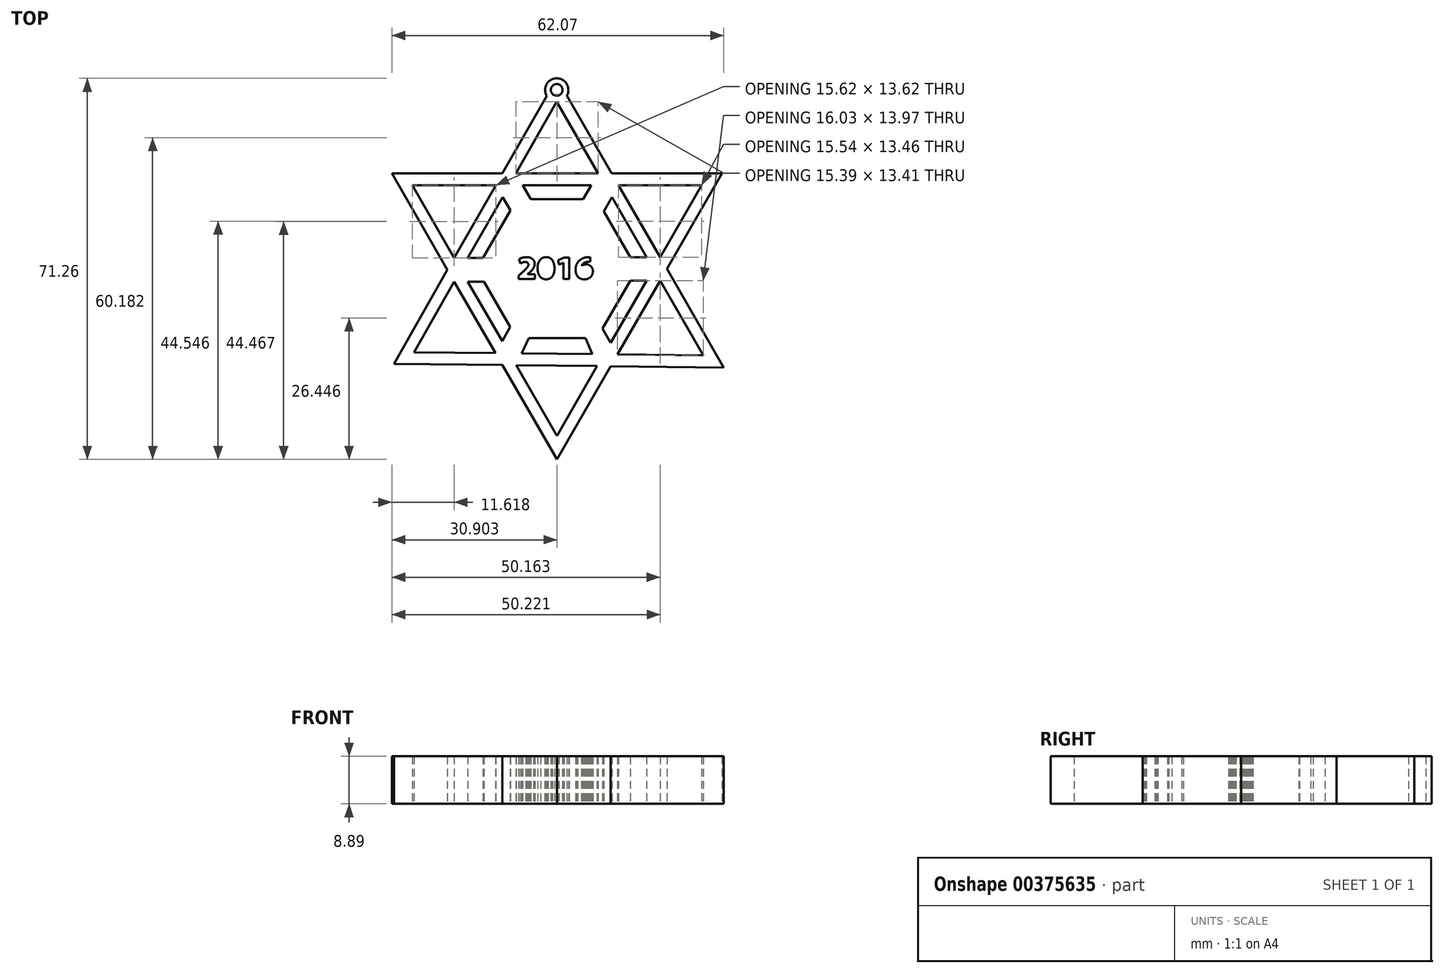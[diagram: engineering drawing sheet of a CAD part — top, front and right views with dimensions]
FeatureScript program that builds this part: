
annotation { "Feature Type Name" : "Feature", "Feature Type Description" : "" }
export const myFeature = defineFeature(function(context is Context, id is Id, definition is map)
    precondition{}
    {
        {
            var Q0;
            Q0=qCreatedBy(makeId("Top.planeOp"),FACE);
            var sketch = newSketch(context, id + "F0", { "sketchPlane" : qUnion([Q0])});
            skLineSegment(sketch, "E0.0", {"start": v(-30.87, 17.82) * mm, "end": v(-10.19, 17.82) * mm});
            skLineSegment(sketch, "E0.1", {"start": v(30.87, 17.82) * mm, "end": v(20.56, -0.03) * mm});
            skLineSegment(sketch, "E0.2", {"start": v(0, -35.65) * mm, "end": v(-10.19, -18) * mm});
            skPoint(sketch, "E0.0.midPoint", {"position": v(0, 17.82) * mm});
            skLineSegment(sketch, "E1.0", {"start": v(31.2, -18.45) * mm, "end": v(10.06, -18.22) * mm});
            skLineSegment(sketch, "E1.1", {"start": v(-30.48, -17.78) * mm, "end": v(-20.46, -0.2) * mm});
            skLineSegment(sketch, "E1.2", {"start": v(-0.03, 35.64) * mm, "end": v(-0.02, 35.61) * mm});
            skLineSegment(sketch, "E2", {"start": v(-27.06, 15.62) * mm, "end": v(-19.2, 2) * mm});
            skLineSegment(sketch, "E3", {"start": v(-27.06, 15.62) * mm, "end": v(-11.44, 15.62) * mm});
            skLineSegment(sketch, "E4", {"start": v(-26.72, -15.6) * mm, "end": v(-19.2, -2.4) * mm});
            skLineSegment(sketch, "E5", {"start": v(-0.02, 31.24) * mm, "end": v(7.73, 17.82) * mm});
            skLineSegment(sketch, "E6", {"start": v(-26.72, -15.6) * mm, "end": v(-11.48, -15.77) * mm});
            skLineSegment(sketch, "E7", {"start": v(27.06, 15.62) * mm, "end": v(19.3, 2.17) * mm});
            skLineSegment(sketch, "E8.trimOffspring", {"start": v(-20.46, -0.2) * mm, "end": v(-30.87, 17.82) * mm});
            skLineSegment(sketch, "E9.trimOffspring", {"start": v(-16.68, 2) * mm, "end": v(-10.17, 13.43) * mm});
            skLineSegment(sketch, "E10.trimOffspring", {"start": v(-16.65, -2.4) * mm, "end": v(-10.23, -13.54) * mm});
            skLineSegment(sketch, "E11.trimOffspring", {"start": v(-19.2, 2) * mm, "end": v(-11.44, 15.62) * mm});
            skPoint(sketch, "E12.orphan", {"position": v(-28.33, 17.82) * mm});
            skLineSegment(sketch, "E13.trimOffspring", {"start": v(-10.19, 17.82) * mm, "end": v(-1.9, 32.35) * mm});
            skLineSegment(sketch, "E14.trimOffspring", {"start": v(-6.4, 15.62) * mm, "end": v(6.46, 15.62) * mm});
            skLineSegment(sketch, "E15.trimOffspring", {"start": v(-7.66, 17.82) * mm, "end": v(-0.02, 31.24) * mm});
            skLineSegment(sketch, "E16.trimOffspring", {"start": v(-7.66, 17.82) * mm, "end": v(7.73, 17.82) * mm});
            skPoint(sketch, "E17.orphan", {"position": v(-1.29, 33.44) * mm});
            skPoint(sketch, "E18.orphan", {"position": v(1.24, 33.44) * mm});
            skLineSegment(sketch, "E19.trimOffspring", {"start": v(10.25, 17.82) * mm, "end": v(30.87, 17.82) * mm});
            skLineSegment(sketch, "E20.trimOffspring", {"start": v(11.52, 15.62) * mm, "end": v(27.06, 15.62) * mm});
            skLineSegment(sketch, "E21.trimOffspring", {"start": v(11.52, 15.62) * mm, "end": v(19.3, 2.17) * mm});
            skLineSegment(sketch, "E22.trimOffspring", {"start": v(10.28, 13.4) * mm, "end": v(16.77, 2.17) * mm});
            skPoint(sketch, "E23.orphan", {"position": v(28.33, 17.82) * mm});
            skPoint(sketch, "E24.orphan", {"position": v(29.6, 15.62) * mm});
            skLineSegment(sketch, "E25.trimOffspring", {"start": v(20.56, -0.03) * mm, "end": v(31.2, -18.45) * mm});
            skLineSegment(sketch, "E26.trimOffspring", {"start": v(19.3, -2.22) * mm, "end": v(27.37, -16.19) * mm});
            skLineSegment(sketch, "E27.trimOffspring", {"start": v(19.3, -2.22) * mm, "end": v(11.34, -16.02) * mm});
            skLineSegment(sketch, "E28.trimOffspring", {"start": v(16.76, -2.22) * mm, "end": v(10.06, -13.82) * mm});
            skPoint(sketch, "E29.orphan", {"position": v(28.66, -18.42) * mm});
            skLineSegment(sketch, "E30.trimOffspring", {"start": v(10.06, -18.22) * mm, "end": v(0, -35.65) * mm});
            skLineSegment(sketch, "E31.trimOffspring", {"start": v(7.54, -18.2) * mm, "end": v(0, -31.25) * mm});
            skLineSegment(sketch, "E32.trimOffspring", {"start": v(11.34, -16.02) * mm, "end": v(27.37, -16.19) * mm});
            skLineSegment(sketch, "E33.trimOffspring", {"start": v(7.54, -18.2) * mm, "end": v(-7.63, -18.03) * mm});
            skLineSegment(sketch, "E34.trimOffspring", {"start": v(-10.19, -18) * mm, "end": v(-30.48, -17.78) * mm});
            skLineSegment(sketch, "E35.trimOffspring", {"start": v(-11.48, -15.77) * mm, "end": v(-19.2, -2.4) * mm});
            skLineSegment(sketch, "E36.trimOffspring", {"start": v(-7.63, -18.03) * mm, "end": v(0, -31.25) * mm});
            skLineSegment(sketch, "E37.trimOffspring", {"start": v(-6.59, -15.82) * mm, "end": v(6.6, -15.96) * mm});
            skPoint(sketch, "E38.orphan", {"position": v(-29.23, -15.58) * mm});
            skLineSegment(sketch, "E39", {"start": v(-0.02, 31.24) * mm, "end": v(-0.03, 35.64) * mm, "construction": true});
            skLineSegment(sketch, "E40", {"start": v(-0.02, 33.44) * mm, "end": v(1.24, 33.44) * mm, "construction": true});
            skArc(sketch, "E41", {"start": v(1.86, 32.36) * mm, "mid": v(-0.03, 35.61) * mm, "end": v(-1.9, 32.35) * mm});
            skCircle(sketch, "E42", {"center": v(-0.02, 33.44) * mm, "radius": 1.1 * mm});
            skLineSegment(sketch, "E43.trimOffspring", {"start": v(-0.05, 35.61) * mm, "end": v(-0.03, 35.64) * mm});
            skLineSegment(sketch, "E44.trimOffspring", {"start": v(1.86, 32.36) * mm, "end": v(10.25, 17.82) * mm});
            skLineSegment(sketch, "E45.0", {"start": v(-4.87, 12.98) * mm, "end": v(4.94, 12.98) * mm});
            skLineSegment(sketch, "E45.1", {"start": v(8.79, 10.75) * mm, "end": v(13.74, 2.17) * mm});
            skLineSegment(sketch, "E45.2", {"start": v(13.71, -2.22) * mm, "end": v(8.54, -11.18) * mm});
            skLineSegment(sketch, "E45.3", {"start": v(5.37, -12.98) * mm, "end": v(-5.25, -12.98) * mm});
            skLineSegment(sketch, "E45.4", {"start": v(-8.72, -10.86) * mm, "end": v(-13.6, -2.4) * mm});
            skLineSegment(sketch, "E45.5", {"start": v(-13.83, 2) * mm, "end": v(-8.7, 10.89) * mm});
            skPoint(sketch, "E45.0.midPoint", {"position": v(0, 12.98) * mm});
            skLineSegment(sketch, "E46", {"start": v(-16.68, 2) * mm, "end": v(-13.83, 2) * mm});
            skLineSegment(sketch, "E47", {"start": v(-16.65, -2.4) * mm, "end": v(-13.6, -2.4) * mm});
            skLineSegment(sketch, "E48", {"start": v(6.46, 15.62) * mm, "end": v(4.94, 12.98) * mm});
            skLineSegment(sketch, "E49", {"start": v(10.28, 13.4) * mm, "end": v(8.79, 10.75) * mm});
            skLineSegment(sketch, "E50", {"start": v(-10.17, 13.43) * mm, "end": v(-8.7, 10.89) * mm});
            skLineSegment(sketch, "E51", {"start": v(-6.4, 15.62) * mm, "end": v(-4.87, 12.98) * mm});
            skLineSegment(sketch, "E52", {"start": v(-10.23, -13.54) * mm, "end": v(-8.72, -10.86) * mm});
            skLineSegment(sketch, "E53", {"start": v(-6.59, -15.82) * mm, "end": v(-5.25, -12.98) * mm});
            skLineSegment(sketch, "E54", {"start": v(6.6, -15.96) * mm, "end": v(5.37, -12.98) * mm});
            skLineSegment(sketch, "E55", {"start": v(10.06, -13.82) * mm, "end": v(8.54, -11.18) * mm});
            skPoint(sketch, "E56.orphan", {"position": v(-15, 0) * mm});
            skPoint(sketch, "E57.orphan", {"position": v(-7.5, 12.98) * mm});
            skPoint(sketch, "E58.orphan", {"position": v(7.5, 12.98) * mm});
            skPoint(sketch, "E59.orphan", {"position": v(-7.5, -12.98) * mm});
            skPoint(sketch, "E60.orphan", {"position": v(7.5, -12.98) * mm});
            skLineSegment(sketch, "E61", {"start": v(16.77, 2.17) * mm, "end": v(13.74, 2.17) * mm});
            skLineSegment(sketch, "E62", {"start": v(16.76, -2.22) * mm, "end": v(13.71, -2.22) * mm});
            skLineSegment(sketch, "E63", {"start": v(-7.09, 1.77) * mm, "end": v(-6.76, 0.94) * mm});
            skLineSegment(sketch, "E64", {"start": v(-7.13, -1.94) * mm, "end": v(-7.13, -1.26) * mm});
            skArc(sketch, "E65", {"start": v(-5.8, 1.27) * mm, "mid": v(-6.32, 1.23) * mm, "end": v(-6.76, 0.94) * mm});
            skArc(sketch, "E66", {"start": v(-5.35, 0.62) * mm, "mid": v(-5.4, 1.06) * mm, "end": v(-5.8, 1.27) * mm});
            skArc(sketch, "E67", {"start": v(-5.76, 0) * mm, "mid": v(-5.52, 0.29) * mm, "end": v(-5.35, 0.62) * mm});
            skArc(sketch, "E68", {"start": v(-7.13, -1.26) * mm, "mid": v(-6.43, -0.65) * mm, "end": v(-5.76, 0) * mm});
            skArc(sketch, "E69", {"start": v(-5.14, 2.11) * mm, "mid": v(-6.15, 2.14) * mm, "end": v(-7.09, 1.77) * mm});
            skArc(sketch, "E70", {"start": v(-4.34, 1.57) * mm, "mid": v(-4.68, 1.93) * mm, "end": v(-5.14, 2.11) * mm});
            skArc(sketch, "E71", {"start": v(-4.34, 0.21) * mm, "mid": v(-4.15, 0.9) * mm, "end": v(-4.34, 1.57) * mm});
            skArc(sketch, "E72", {"start": v(-5.5, -1) * mm, "mid": v(-4.85, -0.46) * mm, "end": v(-4.34, 0.21) * mm});
            skLineSegment(sketch, "E73", {"start": v(-5.5, -1) * mm, "end": v(-4.12, -1) * mm});
            skLineSegment(sketch, "E74", {"start": v(-4.12, -1) * mm, "end": v(-4.12, -1.94) * mm});
            skLineSegment(sketch, "E75", {"start": v(-7.13, -1.94) * mm, "end": v(-4.12, -1.94) * mm});
            skArc(sketch, "E76", {"start": v(-2.36, 1.03) * mm, "mid": v(-2.45, 0.75) * mm, "end": v(-2.47, 0.45) * mm});
            skArc(sketch, "E77", {"start": v(-1.6, 0.45) * mm, "mid": v(-1.6, 0.75) * mm, "end": v(-1.7, 1.05) * mm});
            skArc(sketch, "E78", {"start": v(-2.11, 1.33) * mm, "mid": v(-2.27, 1.2) * mm, "end": v(-2.36, 1.03) * mm});
            skArc(sketch, "E79", {"start": v(-1.7, 1.05) * mm, "mid": v(-1.78, 1.2) * mm, "end": v(-1.91, 1.33) * mm});
            skArc(sketch, "E80", {"start": v(-1.91, 1.33) * mm, "mid": v(-2.01, 1.34) * mm, "end": v(-2.11, 1.33) * mm});
            skArc(sketch, "E81", {"start": v(-2.36, -0.83) * mm, "mid": v(-2.27, -1) * mm, "end": v(-2.11, -1.1) * mm});
            skArc(sketch, "E82", {"start": v(-1.9, -1.1) * mm, "mid": v(-1.76, -1) * mm, "end": v(-1.7, -0.83) * mm});
            skArc(sketch, "E83", {"start": v(-2.11, -1.1) * mm, "mid": v(-2, -1.14) * mm, "end": v(-1.9, -1.1) * mm});
            skArc(sketch, "E84", {"start": v(-2.48, -0.29) * mm, "mid": v(-2.44, -0.56) * mm, "end": v(-2.36, -0.83) * mm});
            skArc(sketch, "E85", {"start": v(-1.7, -0.83) * mm, "mid": v(-1.62, -0.56) * mm, "end": v(-1.57, -0.3) * mm});
            skLineSegment(sketch, "E86", {"start": v(-2.48, -0.29) * mm, "end": v(-2.47, 0.45) * mm});
            skLineSegment(sketch, "E87", {"start": v(-1.57, -0.3) * mm, "end": v(-1.6, 0.45) * mm});
            skLineSegment(sketch, "E88", {"start": v(0.24, 1.61) * mm, "end": v(0.4, 0.79) * mm});
            skLineSegment(sketch, "E89", {"start": v(0.4, 0.79) * mm, "end": v(1.22, 1.12) * mm});
            skLineSegment(sketch, "E90", {"start": v(1.22, 1.12) * mm, "end": v(1.22, -1.92) * mm});
            skLineSegment(sketch, "E91", {"start": v(1.22, -1.92) * mm, "end": v(2.32, -1.92) * mm});
            skLineSegment(sketch, "E92", {"start": v(2.32, -1.92) * mm, "end": v(2.32, 2.1) * mm});
            skLineSegment(sketch, "E93", {"start": v(2.32, 2.1) * mm, "end": v(1.38, 2.1) * mm});
            skLineSegment(sketch, "E94", {"start": v(1.38, 2.1) * mm, "end": v(0.24, 1.61) * mm});
            skArc(sketch, "E95", {"start": v(-3.04, 1.77) * mm, "mid": v(-3.46, 1.15) * mm, "end": v(-3.6, 0.4) * mm});
            skArc(sketch, "E96", {"start": v(-2.24, 2.16) * mm, "mid": v(-2.67, 2.03) * mm, "end": v(-3.04, 1.77) * mm});
            skArc(sketch, "E97", {"start": v(-1.66, 2.16) * mm, "mid": v(-1.95, 2.18) * mm, "end": v(-2.24, 2.16) * mm});
            skArc(sketch, "E98", {"start": v(-0.82, 1.56) * mm, "mid": v(-1.18, 1.95) * mm, "end": v(-1.66, 2.16) * mm});
            skArc(sketch, "E99", {"start": v(-0.45, 0) * mm, "mid": v(-0.52, 0.8) * mm, "end": v(-0.82, 1.56) * mm});
            skArc(sketch, "E100", {"start": v(-1.01, -1.61) * mm, "mid": v(-0.58, -0.86) * mm, "end": v(-0.45, 0) * mm});
            skArc(sketch, "E101", {"start": v(-1.92, -1.98) * mm, "mid": v(-1.43, -1.88) * mm, "end": v(-1.01, -1.61) * mm});
            skArc(sketch, "E102", {"start": v(-3.04, -1.6) * mm, "mid": v(-2.52, -1.9) * mm, "end": v(-1.92, -1.98) * mm});
            skArc(sketch, "E103", {"start": v(-3.58, -0.22) * mm, "mid": v(-3.44, -0.97) * mm, "end": v(-3.04, -1.6) * mm});
            skArc(sketch, "E104", {"start": v(-3.6, 0.4) * mm, "mid": v(-3.6, 0.09) * mm, "end": v(-3.58, -0.22) * mm});
            skArc(sketch, "E105", {"start": v(5.48, -0.17) * mm, "mid": v(5.04, 0) * mm, "end": v(4.65, -0.26) * mm});
            skArc(sketch, "E106", {"start": v(4.65, -0.26) * mm, "mid": v(4.67, -0.75) * mm, "end": v(4.98, -1.13) * mm});
            skArc(sketch, "E107", {"start": v(4.98, -1.13) * mm, "mid": v(5.33, -1.12) * mm, "end": v(5.53, -0.83) * mm});
            skArc(sketch, "E108", {"start": v(5.53, -0.83) * mm, "mid": v(5.58, -0.5) * mm, "end": v(5.48, -0.17) * mm});
            skArc(sketch, "E109", {"start": v(5.1, 1.12) * mm, "mid": v(4.82, 0.9) * mm, "end": v(4.66, 0.58) * mm});
            skArc(sketch, "E110", {"start": v(6.26, 1.3) * mm, "mid": v(5.67, 1.28) * mm, "end": v(5.1, 1.12) * mm});
            skArc(sketch, "E111", {"start": v(5.46, 0.8) * mm, "mid": v(5.04, 0.76) * mm, "end": v(4.66, 0.58) * mm});
            skArc(sketch, "E112", {"start": v(6.19, 0.58) * mm, "mid": v(5.85, 0.77) * mm, "end": v(5.46, 0.8) * mm});
            skArc(sketch, "E113", {"start": v(6.72, -0.22) * mm, "mid": v(6.55, 0.25) * mm, "end": v(6.19, 0.58) * mm});
            skArc(sketch, "E114", {"start": v(6.6, -1.1) * mm, "mid": v(6.71, -0.67) * mm, "end": v(6.72, -0.22) * mm});
            skArc(sketch, "E115", {"start": v(6, -1.78) * mm, "mid": v(6.36, -1.49) * mm, "end": v(6.6, -1.1) * mm});
            skArc(sketch, "E116", {"start": v(5.01, -1.99) * mm, "mid": v(5.52, -1.95) * mm, "end": v(6, -1.78) * mm});
            skArc(sketch, "E117", {"start": v(3.92, -1.48) * mm, "mid": v(4.42, -1.84) * mm, "end": v(5.01, -1.99) * mm});
            skArc(sketch, "E118", {"start": v(3.5, -0.3) * mm, "mid": v(3.61, -0.93) * mm, "end": v(3.92, -1.48) * mm});
            skArc(sketch, "E119", {"start": v(3.75, 0.94) * mm, "mid": v(3.54, 0.34) * mm, "end": v(3.5, -0.3) * mm});
            skArc(sketch, "E120", {"start": v(4.57, 1.81) * mm, "mid": v(4.1, 1.44) * mm, "end": v(3.75, 0.94) * mm});
            skArc(sketch, "E121", {"start": v(5.76, 2.15) * mm, "mid": v(5.14, 2.07) * mm, "end": v(4.57, 1.81) * mm});
            skLineSegment(sketch, "E122", {"start": v(5.7, 2.15) * mm, "end": v(6.27, 2.15) * mm});
            skLineSegment(sketch, "E123", {"start": v(6.27, 2.15) * mm, "end": v(6.26, 1.3) * mm});
            skPoint(sketch, "E124.orphan", {"position": v(6.19, 2.1) * mm});
            skSolve(sketch);
        }
        {
            var Q0;
            Q0=makeQuery(id+"F0.imprint","IMPRINT",FACE,{"disambiguationData":[TD([[makeQuery(id+"F0.imprint","IMPRINT",EDGE,{"derivedFrom":sQuery(id+"F0.wireOp",EDGE,"E0.0")}),-1.0]])]});
            extrude(context, id + "F1", {"entities" : qUnion([Q0]), "depth" : 8.9 * mm});
        }
    });
